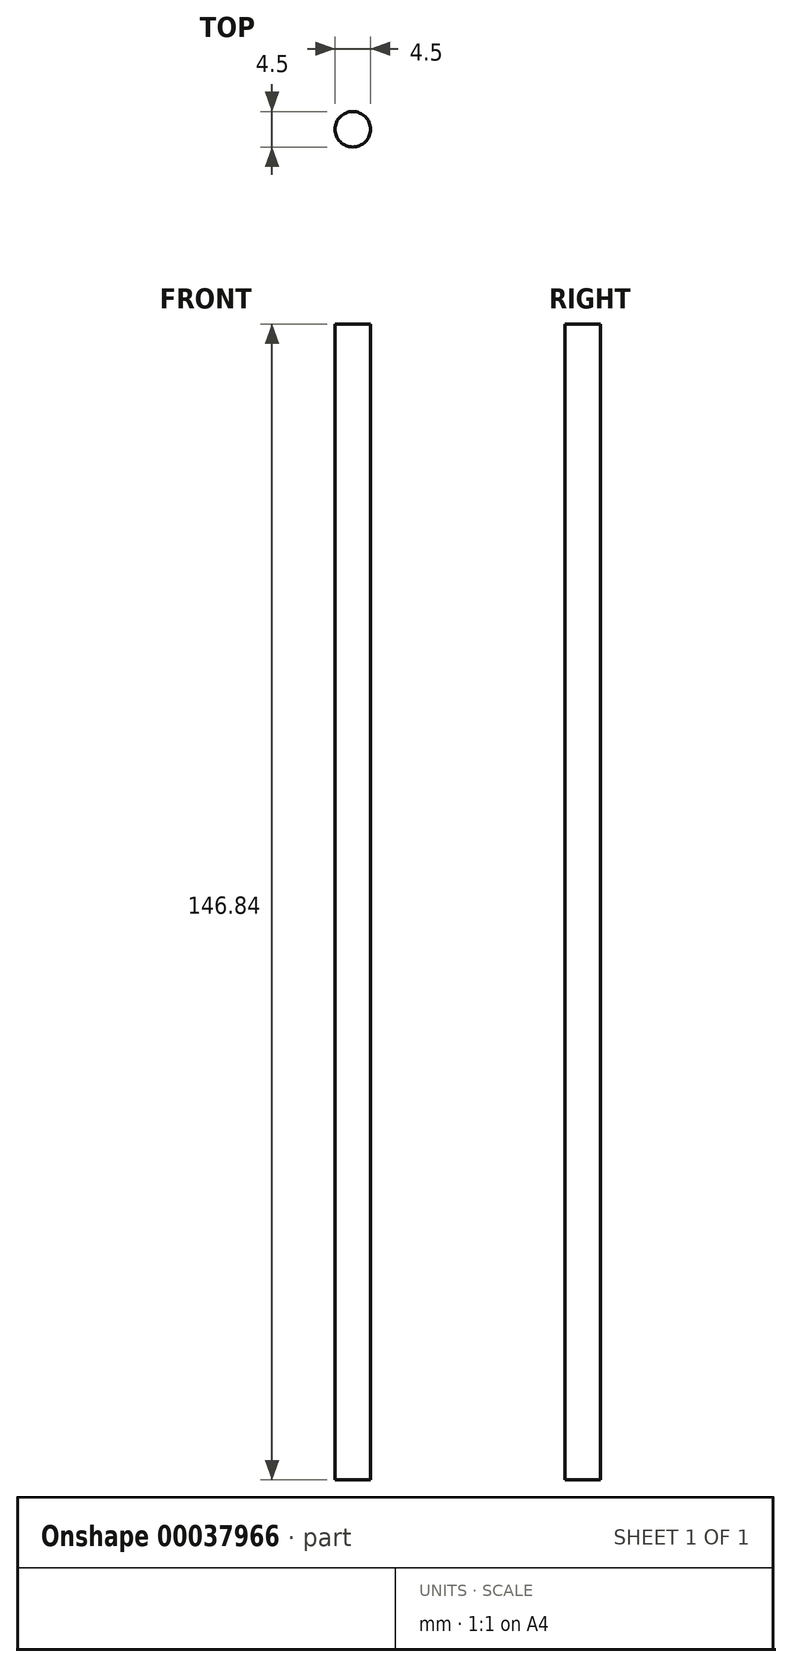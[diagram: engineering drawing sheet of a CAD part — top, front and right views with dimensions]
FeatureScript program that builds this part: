
annotation { "Feature Type Name" : "Feature", "Feature Type Description" : "" }
export const myFeature = defineFeature(function(context is Context, id is Id, definition is map)
    precondition{}
    {
        {
            var Q0;
            Q0=qCreatedBy(makeId("Top.planeOp"),FACE);
            var sketch = newSketch(context, id + "F0", { "sketchPlane" : qUnion([Q0])});
            skCircle(sketch, "E0", {"center": v(0, 0) * mm, "radius": 2.25 * mm});
            skSolve(sketch);
        }
        {
            var Q0;
            Q0=qSketchRegion(id+"F0",true);
            extrude(context, id + "F1", {"entities" : qUnion([Q0]), "depth" : 146.84 * mm});
        }
    });
